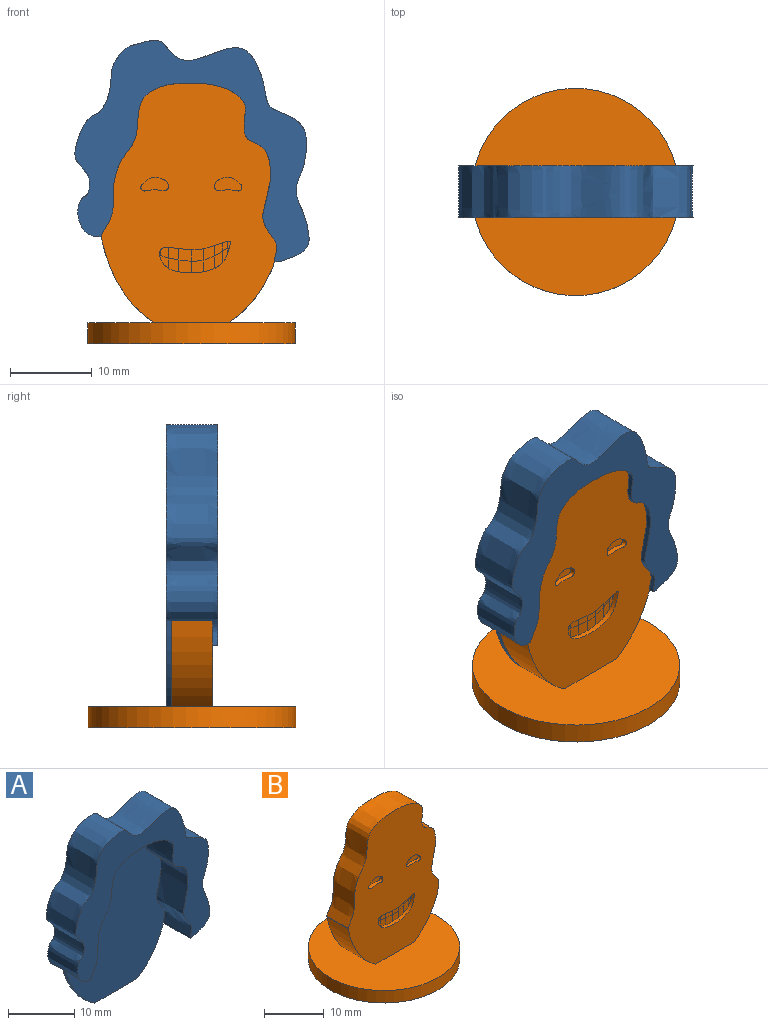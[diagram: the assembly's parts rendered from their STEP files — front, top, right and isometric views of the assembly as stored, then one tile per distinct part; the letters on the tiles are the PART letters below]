
ASSEMBLY  parts=2 mates=1
PART A: 11 faces, bbox 28.9x6.4x34.7 mm
  f0: extruded ~21.88x21.51mm, area 313.2mm2, adj f1,f4,f5,f10
  f1: extruded ~6.35x0.78mm, area 5mm2, adj f0,f2,f5,f6,f9
  f2: extruded ~6.35x1.04mm, area 6.9mm2, adj f1,f3,f5,f6
  f3: extruded ~28.56x26.56mm, area 491mm2, adj f2,f4,f5,f6,f8
  f4: extruded ~5.72x0.09mm, area 0.6mm2, adj f0,f3,f5,f10
  f5: plane 28.89x27.21mm, normal (0,-1,0), area 257.1mm2, adj f0,f1,f2,f3,f4
  f6: plane 34.68x28.89mm, normal (0,1,0), area 743.4mm2, adj f1,f2,f3,f7,f8,f9
  f7: plane 8.96x0.64mm, normal (0,0,-1), area 5.7mm2, adj f6,f8,f9,f10
  f8: extruded ~10.54x6.57mm, area 8.1mm2, adj f3,f6,f7,f10
  f9: extruded ~7.48x5.73mm, area 6.1mm2, adj f1,f6,f7,f10
  f10: plane 29.39x21.63mm, normal (0,-1,0), area 486.3mm2, adj f0,f4,f7,f8,f9
PART B: 32 faces, bbox 25.4x25.4x31.9 mm
  f0: plane 29.39x21.63mm, normal (0,-1,0), area 455.4mm2, adj f1,f2,f21,f22,f23,f25,f27,f30
  f1: extruded ~7.48x5.73mm, area 48.8mm2, adj f0,f3,f22,f30
  f2: extruded ~10.54x6.57mm, area 64.9mm2, adj f0,f3,f21,f30
  f3: plane 29.39x21.63mm, normal (0,1,0), area 486.3mm2, adj f1,f2,f21,f22,f30
  f4: plane 0.84x0.37mm, normal (0,-1,0), area 0.2mm2, adj f5,f13,f27
  f5: plane 1.23x0.64mm, normal (0,-1,0), area 0.6mm2, adj f4,f9,f14,f27
  f6: plane 0.51x0.1mm, normal (0,-1,0), area 0mm2, adj f8,f27,f28
  f7: plane 1.77x1.29mm, normal (0,-1,0), area 1.7mm2, adj f9,f11,f16,f27
  f8: plane 1.33x1.05mm, normal (0,-1,0), area 1.1mm2, adj f6,f10,f19,f27
  f9: plane 1.64x1.03mm, normal (0,-1,0), area 1.2mm2, adj f5,f7,f15,f27
  f10: plane 1.56x1.29mm, normal (0,-1,0), area 1.7mm2, adj f8,f12,f20,f27
  f11: plane 1.56x1.54mm, normal (0,-1,0), area 2.1mm2, adj f7,f12,f17,f27
  f12: plane 1.56x1.54mm, normal (0,-1,0), area 2.1mm2, adj f10,f11,f18,f27
  f13: plane 0.81x0.24mm, normal (0,-1,0), area 0.1mm2, adj f4,f14,f27
  f14: plane 1.81x0.65mm, normal (0,-1,0), area 0.7mm2, adj f5,f13,f15,f27
  f15: plane 2.13x1.04mm, normal (0,-1,0), area 1.5mm2, adj f9,f14,f16,f27
  f16: plane 1.95x1.29mm, normal (0,-1,0), area 1.9mm2, adj f7,f15,f17,f27
  f17: plane 1.61x1.54mm, normal (0,-1,0), area 2.2mm2, adj f11,f16,f18,f27
  f18: plane 1.59x1.54mm, normal (0,-1,0), area 2.2mm2, adj f12,f17,f20,f27
  f19: plane 1.73x1.04mm, normal (0,-1,0), area 1mm2, adj f8,f20,f27,f28
  f20: plane 1.73x1.29mm, normal (0,-1,0), area 1.8mm2, adj f10,f18,f19,f27
  f21: extruded ~5.08x0.09mm, area 0.5mm2, adj f0,f2,f3,f22
  f22: extruded ~21.88x21.51mm, area 278.4mm2, adj f0,f1,f3,f21
  f23: extruded ~3.35x1.67mm, area 5.3mm2, adj f0,f24
  f24: plane 3.42x1.73mm, normal (0,-1,0), area 4.3mm2, adj f23
  f25: extruded ~3.35x1.67mm, area 5.3mm2, adj f0,f26
  f26: plane 3.42x1.73mm, normal (0,-1,0), area 4.3mm2, adj f25
  f27: extruded ~8.68x3.89mm, area 13.6mm2, adj f0,f4,f5,f6,f7,f8,f9,f10
  f28: plane 0.57x0.1mm, normal (0,-1,0), area 0mm2, adj f6,f19,f27
  f29: cylinder r=12.7mm len=25.4mm, axis (0,0,1), area 202.7mm2, adj f30,f31
  f30: plane 25.4x25.4mm, normal (0,0,1), area 461.2mm2, adj f0,f1,f2,f3,f29
  f31: plane 25.4x25.4mm, normal (0,0,-1), area 506.7mm2, adj f29
PLACE A t=(0,0,1.27)mm
PLACE B t=(0,0,1.27)mm
MATE fastened A.f10 <-> B.f3  axis (0,-1,0) through (-0.05,2.54,16.46)mm
